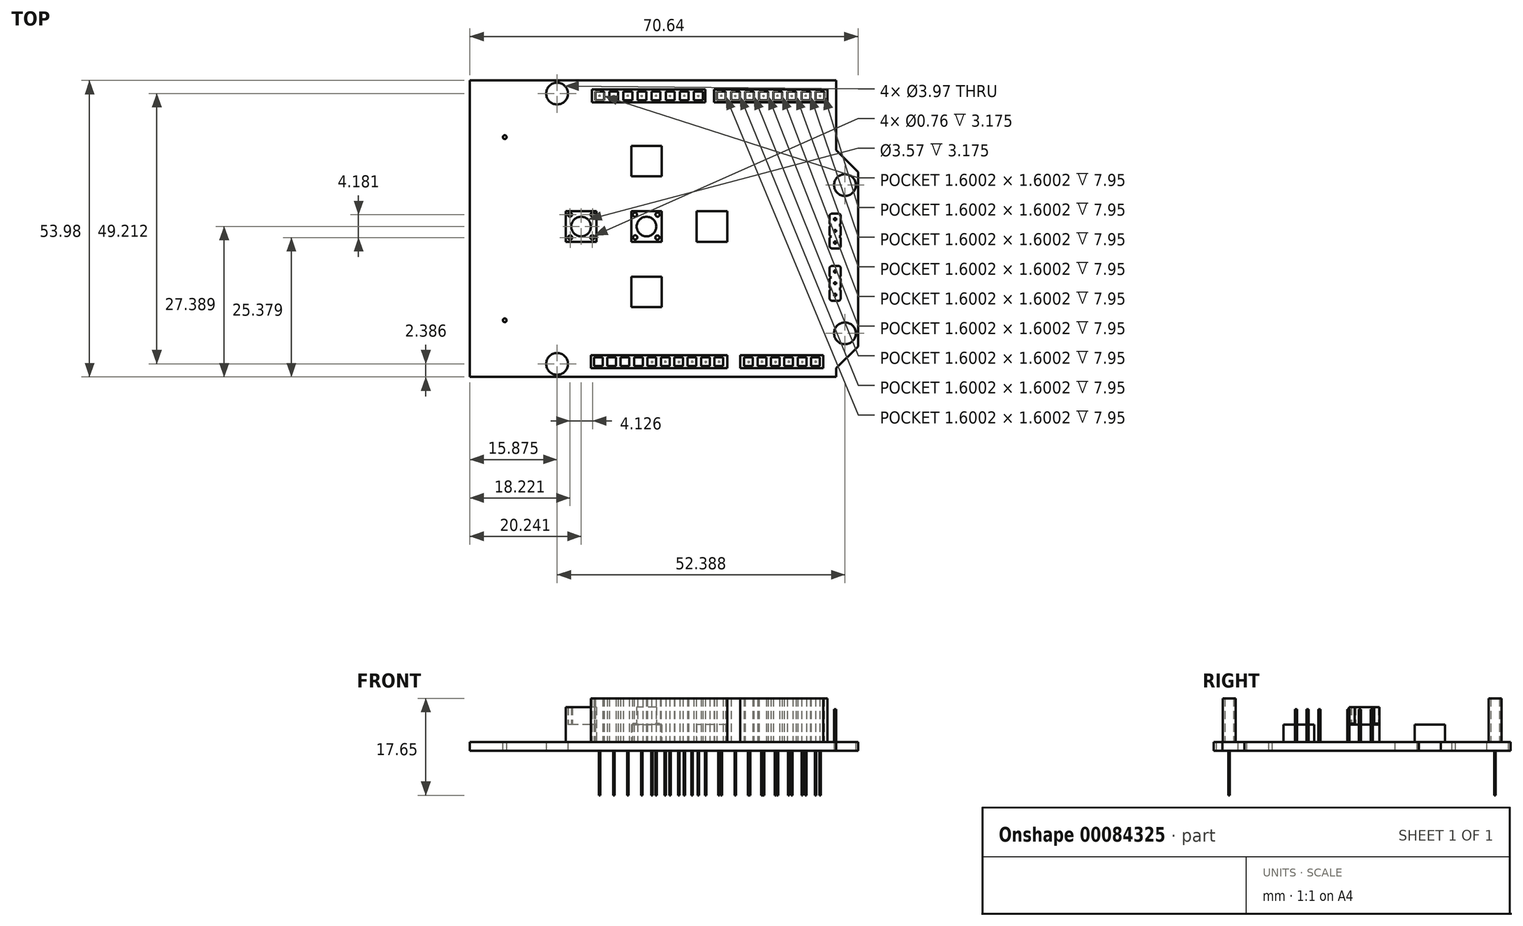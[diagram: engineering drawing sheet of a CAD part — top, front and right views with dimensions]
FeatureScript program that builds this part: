
annotation { "Feature Type Name" : "Feature", "Feature Type Description" : "" }
export const myFeature = defineFeature(function(context is Context, id is Id, definition is map)
    precondition{}
    {
        {
            var Q0;
            Q0=qCreatedBy(makeId("Top.planeOp"),FACE);
            var sketch = newSketch(context, id + "F0", { "sketchPlane" : qUnion([Q0])});
            skLineSegment(sketch, "E0.bottom", {"start": v(0, 0) * mm, "end": v(66.68, 0) * mm});
            skLineSegment(sketch, "E0.top", {"start": v(0, -53.98) * mm, "end": v(66.68, -53.98) * mm});
            skLineSegment(sketch, "E0.left", {"start": v(0, 0) * mm, "end": v(0, -53.98) * mm});
            skLineSegment(sketch, "E0.right", {"start": v(66.68, 0) * mm, "end": v(66.68, -53.97) * mm});
            skLineSegment(sketch, "E1", {"start": v(66.68, -12.7) * mm, "end": v(70.64, -16.67) * mm});
            skLineSegment(sketch, "E2", {"start": v(70.64, -16.67) * mm, "end": v(70.64, -48.42) * mm});
            skLineSegment(sketch, "E3", {"start": v(70.64, -48.42) * mm, "end": v(66.68, -52.39) * mm});
            skCircle(sketch, "E4", {"center": v(68.26, -19.05) * mm, "radius": 1.98 * mm});
            skLineSegment(sketch, "E5", {"start": v(66.68, -12.7) * mm, "end": v(68.26, -12.7) * mm, "construction": true});
            skLineSegment(sketch, "E6", {"start": v(68.26, -12.7) * mm, "end": v(68.26, -19.05) * mm, "construction": true});
            skLineSegment(sketch, "E7", {"start": v(70.64, -32.54) * mm, "end": v(66.68, -32.54) * mm});
            skCircle(sketch, "E8.MirrorC", {"center": v(68.26, -46.04) * mm, "radius": 1.98 * mm});
            skCircle(sketch, "E9", {"center": v(15.88, -2.38) * mm, "radius": 1.98 * mm});
            skLineSegment(sketch, "E10", {"start": v(0, -26.99) * mm, "end": v(15.88, -26.99) * mm, "construction": true});
            skCircle(sketch, "E11.MirrorC", {"center": v(15.88, -51.6) * mm, "radius": 1.98 * mm});
            skSolve(sketch);
        }
        {
            var Q0;
            {var subQ7=sQuery(id+"F0.wireOp",EDGE,"E0.bottom");Q0=makeQuery(id+"F0.imprint","IMPRINT",FACE,{"disambiguationData":[TD([[makeQuery(id+"F0.imprint","IMPRINT",EDGE,{"derivedFrom":subQ7}),-1.0]])]});}
            var Q1;
            {var subQ1=sQuery(id+"F0.wireOp",EDGE,"E1");Q1=makeQuery(id+"F0.imprint","IMPRINT",FACE,{"disambiguationData":[TD([[makeQuery(id+"F0.imprint","IMPRINT",EDGE,{"derivedFrom":subQ1}),-1.0]])]});}
            var Q2;
            {var subQ0=sQuery(id+"F0.wireOp",EDGE,"E3");Q2=makeQuery(id+"F0.imprint","IMPRINT",FACE,{"disambiguationData":[TD([[makeQuery(id+"F0.imprint","IMPRINT",EDGE,{"derivedFrom":subQ0}),-1.0]])]});}
            extrude(context, id + "F1", {"entities" : qUnion([Q0, Q1, Q2]), "depth" : 1.6 * mm});
        }
        {
            var Q0;
            Q0=makeQuery(id+"F1.opExtrude","CAP_FACE",FACE,{"disambiguationData":[OSD([sQuery(id+"F0.wireOp",EDGE,"E0.bottom"),sQuery(id+"F0.wireOp",EDGE,"E0.top"),sQuery(id+"F0.wireOp",EDGE,"E0.left"),sQuery(id+"F0.wireOp",EDGE,"E0.right"),sQuery(id+"F0.wireOp",EDGE,"E1"),sQuery(id+"F0.wireOp",EDGE,"E2"),sQuery(id+"F0.wireOp",EDGE,"E3"),sQuery(id+"F0.wireOp",EDGE,"E4"),sQuery(id+"F0.wireOp",EDGE,"E8.MirrorC"),sQuery(id+"F0.wireOp",EDGE,"E9"),sQuery(id+"F0.wireOp",EDGE,"E11.MirrorC")])],"isStart":false});
            var sketch = newSketch(context, id + "F2", { "sketchPlane" : qUnion([Q0])});
            skLineSegment(sketch, "E12.bottom", {"start": v(22.24, -1.6) * mm, "end": v(42.88, -1.6) * mm});
            skLineSegment(sketch, "E12.top", {"start": v(22.24, -3.99) * mm, "end": v(42.88, -3.99) * mm});
            skLineSegment(sketch, "E12.left", {"start": v(22.24, -1.6) * mm, "end": v(22.24, -3.99) * mm});
            skLineSegment(sketch, "E12.right", {"start": v(42.88, -1.6) * mm, "end": v(42.88, -3.99) * mm});
            skLineSegment(sketch, "E13.bottom", {"start": v(22.82, -2) * mm, "end": v(24.42, -2) * mm});
            skLineSegment(sketch, "E13.top", {"start": v(22.82, -3.6) * mm, "end": v(24.42, -3.6) * mm});
            skLineSegment(sketch, "E13.left", {"start": v(22.82, -2) * mm, "end": v(22.82, -3.6) * mm});
            skLineSegment(sketch, "E13.right", {"start": v(24.42, -2) * mm, "end": v(24.42, -3.6) * mm});
            skLineSegment(sketch, "E14", {"start": v(24.9, -1.6) * mm, "end": v(24.9, -3.99) * mm, "construction": true});
            skLineSegment(sketch, "E15.MirrorCS", {"start": v(25.39, -2) * mm, "end": v(25.39, -3.6) * mm});
            skLineSegment(sketch, "E16.MirrorCS", {"start": v(26.99, -2) * mm, "end": v(25.39, -2) * mm});
            skLineSegment(sketch, "E17.MirrorCS", {"start": v(26.99, -2) * mm, "end": v(26.99, -3.6) * mm});
            skLineSegment(sketch, "E18.MirrorCS", {"start": v(26.99, -3.6) * mm, "end": v(25.39, -3.6) * mm});
            skLineSegment(sketch, "E19", {"start": v(27.47, -1.6) * mm, "end": v(27.47, -3.99) * mm, "construction": true});
            skLineSegment(sketch, "E20.MirrorCS", {"start": v(27.95, -2) * mm, "end": v(27.95, -3.6) * mm});
            skLineSegment(sketch, "E21.MirrorCS", {"start": v(27.95, -2) * mm, "end": v(29.55, -2) * mm});
            skLineSegment(sketch, "E22.MirrorCS", {"start": v(29.55, -2) * mm, "end": v(29.55, -3.6) * mm});
            skLineSegment(sketch, "E23.MirrorCS", {"start": v(27.95, -3.6) * mm, "end": v(29.55, -3.6) * mm});
            skLineSegment(sketch, "E24.MirrorCS", {"start": v(30.52, -2) * mm, "end": v(30.52, -3.6) * mm});
            skLineSegment(sketch, "E25.MirrorCS", {"start": v(32.12, -2) * mm, "end": v(30.52, -2) * mm});
            skLineSegment(sketch, "E26.MirrorCS", {"start": v(32.12, -2) * mm, "end": v(32.12, -3.6) * mm});
            skLineSegment(sketch, "E27.MirrorCS", {"start": v(32.12, -3.6) * mm, "end": v(30.52, -3.6) * mm});
            skLineSegment(sketch, "E28", {"start": v(32.6, -1.6) * mm, "end": v(32.6, -3.99) * mm, "construction": true});
            skLineSegment(sketch, "E29.MirrorCS", {"start": v(33.08, -2) * mm, "end": v(33.08, -3.6) * mm});
            skLineSegment(sketch, "E30.MirrorCS", {"start": v(33.08, -2) * mm, "end": v(34.68, -2) * mm});
            skLineSegment(sketch, "E31.MirrorCS", {"start": v(34.68, -2) * mm, "end": v(34.68, -3.6) * mm});
            skLineSegment(sketch, "E32.MirrorCS", {"start": v(33.08, -3.6) * mm, "end": v(34.68, -3.6) * mm});
            skLineSegment(sketch, "E33.MirrorCS", {"start": v(35.65, -2) * mm, "end": v(35.65, -3.6) * mm});
            skLineSegment(sketch, "E34.MirrorCS", {"start": v(37.25, -2) * mm, "end": v(35.65, -2) * mm});
            skLineSegment(sketch, "E35.MirrorCS", {"start": v(37.25, -2) * mm, "end": v(37.25, -3.6) * mm});
            skLineSegment(sketch, "E36.MirrorCS", {"start": v(37.25, -3.6) * mm, "end": v(35.65, -3.6) * mm});
            skLineSegment(sketch, "E37.MirrorCS", {"start": v(38.21, -2) * mm, "end": v(38.21, -3.6) * mm});
            skLineSegment(sketch, "E38.MirrorCS", {"start": v(38.21, -2) * mm, "end": v(39.81, -2) * mm});
            skLineSegment(sketch, "E39.MirrorCS", {"start": v(39.81, -2) * mm, "end": v(39.81, -3.6) * mm});
            skLineSegment(sketch, "E40.MirrorCS", {"start": v(38.21, -3.6) * mm, "end": v(39.81, -3.6) * mm});
            skLineSegment(sketch, "E41.MirrorCS", {"start": v(40.78, -2) * mm, "end": v(40.78, -3.6) * mm});
            skLineSegment(sketch, "E42.MirrorCS", {"start": v(42.38, -2) * mm, "end": v(40.78, -2) * mm});
            skLineSegment(sketch, "E43.MirrorCS", {"start": v(42.38, -2) * mm, "end": v(42.38, -3.6) * mm});
            skLineSegment(sketch, "E44.MirrorCS", {"start": v(42.38, -3.6) * mm, "end": v(40.78, -3.6) * mm});
            skLineSegment(sketch, "E45", {"start": v(43.67, -3.99) * mm, "end": v(43.67, -6.48) * mm, "construction": true});
            skLineSegment(sketch, "E46.MirrorCS", {"start": v(44.46, -1.6) * mm, "end": v(44.46, -3.99) * mm});
            skLineSegment(sketch, "E47.MirrorCS", {"start": v(65.1, -1.6) * mm, "end": v(65.1, -3.99) * mm});
            skLineSegment(sketch, "E48.MirrorCS", {"start": v(65.1, -1.6) * mm, "end": v(44.46, -1.6) * mm});
            skLineSegment(sketch, "E49.MirrorCS", {"start": v(65.1, -3.99) * mm, "end": v(44.46, -3.99) * mm});
            skLineSegment(sketch, "E50.MirrorCS", {"start": v(44.96, -3.6) * mm, "end": v(46.56, -3.6) * mm});
            skLineSegment(sketch, "E51.MirrorCS", {"start": v(44.96, -2) * mm, "end": v(44.96, -3.6) * mm});
            skLineSegment(sketch, "E52.MirrorCS", {"start": v(44.96, -2) * mm, "end": v(46.56, -2) * mm});
            skLineSegment(sketch, "E53.MirrorCS", {"start": v(46.56, -2) * mm, "end": v(46.56, -3.6) * mm});
            skLineSegment(sketch, "E54.MirrorCS", {"start": v(47.52, -2) * mm, "end": v(47.52, -3.6) * mm});
            skLineSegment(sketch, "E55.MirrorCS", {"start": v(49.12, -2) * mm, "end": v(47.52, -2) * mm});
            skLineSegment(sketch, "E56.MirrorCS", {"start": v(49.12, -2) * mm, "end": v(49.12, -3.6) * mm});
            skLineSegment(sketch, "E57.MirrorCS", {"start": v(49.12, -3.6) * mm, "end": v(47.52, -3.6) * mm});
            skLineSegment(sketch, "E58.MirrorCS", {"start": v(50.09, -2) * mm, "end": v(50.09, -3.6) * mm});
            skLineSegment(sketch, "E59.MirrorCS", {"start": v(50.09, -2) * mm, "end": v(51.69, -2) * mm});
            skLineSegment(sketch, "E60.MirrorCS", {"start": v(51.69, -2) * mm, "end": v(51.69, -3.6) * mm});
            skLineSegment(sketch, "E61.MirrorCS", {"start": v(50.09, -3.6) * mm, "end": v(51.69, -3.6) * mm});
            skLineSegment(sketch, "E62.MirrorCS", {"start": v(52.65, -2) * mm, "end": v(52.65, -3.6) * mm});
            skLineSegment(sketch, "E63.MirrorCS", {"start": v(54.25, -2) * mm, "end": v(52.65, -2) * mm});
            skLineSegment(sketch, "E64.MirrorCS", {"start": v(54.25, -2) * mm, "end": v(54.25, -3.6) * mm});
            skLineSegment(sketch, "E65.MirrorCS", {"start": v(54.25, -3.6) * mm, "end": v(52.65, -3.6) * mm});
            skLineSegment(sketch, "E66.MirrorCS", {"start": v(55.22, -2) * mm, "end": v(55.22, -3.6) * mm});
            skLineSegment(sketch, "E67.MirrorCS", {"start": v(55.22, -2) * mm, "end": v(56.82, -2) * mm});
            skLineSegment(sketch, "E68.MirrorCS", {"start": v(56.82, -2) * mm, "end": v(56.82, -3.6) * mm});
            skLineSegment(sketch, "E69.MirrorCS", {"start": v(55.22, -3.6) * mm, "end": v(56.82, -3.6) * mm});
            skLineSegment(sketch, "E70.MirrorCS", {"start": v(57.79, -2) * mm, "end": v(57.79, -3.6) * mm});
            skLineSegment(sketch, "E71.MirrorCS", {"start": v(59.39, -2) * mm, "end": v(57.79, -2) * mm});
            skLineSegment(sketch, "E72.MirrorCS", {"start": v(59.39, -2) * mm, "end": v(59.39, -3.6) * mm});
            skLineSegment(sketch, "E73.MirrorCS", {"start": v(59.39, -3.6) * mm, "end": v(57.79, -3.6) * mm});
            skLineSegment(sketch, "E74.MirrorCS", {"start": v(60.35, -2) * mm, "end": v(60.35, -3.6) * mm});
            skLineSegment(sketch, "E75.MirrorCS", {"start": v(60.35, -2) * mm, "end": v(61.95, -2) * mm});
            skLineSegment(sketch, "E76.MirrorCS", {"start": v(61.95, -2) * mm, "end": v(61.95, -3.6) * mm});
            skLineSegment(sketch, "E77.MirrorCS", {"start": v(60.35, -3.6) * mm, "end": v(61.95, -3.6) * mm});
            skLineSegment(sketch, "E78.MirrorCS", {"start": v(62.92, -2) * mm, "end": v(62.92, -3.6) * mm});
            skLineSegment(sketch, "E79.MirrorCS", {"start": v(64.52, -2) * mm, "end": v(62.92, -2) * mm});
            skLineSegment(sketch, "E80.MirrorCS", {"start": v(64.52, -2) * mm, "end": v(64.52, -3.6) * mm});
            skLineSegment(sketch, "E81.MirrorCS", {"start": v(64.52, -3.6) * mm, "end": v(62.92, -3.6) * mm});
            skSolve(sketch);
        }
        {
            var Q0;
            Q0=makeQuery(id+"F2.imprint","IMPRINT",FACE,{"disambiguationData":[TD([[makeQuery(id+"F2.imprint","IMPRINT",EDGE,{"derivedFrom":sQuery(id+"F2.wireOp",EDGE,"E12.bottom")}),-1.0]])]});
            var Q1;
            Q1=makeQuery(id+"F2.imprint","IMPRINT",FACE,{"disambiguationData":[TD([[makeQuery(id+"F2.imprint","IMPRINT",EDGE,{"derivedFrom":sQuery(id+"F2.wireOp",EDGE,"E46.MirrorCS")}),1.0]])]});
            extrude(context, id + "F3", {"entities" : qUnion([Q0, Q1]), "operationType" : NewBodyOperationType.ADD, "depth" : 7.95 * mm});
        }
        {
            var Q0;
            {var subQ0=sQuery(id+"F0.wireOp",EDGE,"E8.MirrorC");var subQ1=sQuery(id+"F0.wireOp",EDGE,"E3");var subQ2=sQuery(id+"F0.wireOp",EDGE,"E2");var subQ3=sQuery(id+"F0.wireOp",EDGE,"E1");var subQ4=sQuery(id+"F0.wireOp",EDGE,"E0.right");var subQ5=sQuery(id+"F0.wireOp",EDGE,"E0.top");var subQ6=sQuery(id+"F0.wireOp",EDGE,"E0.bottom");var subQ7=sQuery(id+"F0.wireOp",EDGE,"E4");var subQ8=sQuery(id+"F0.wireOp",EDGE,"E0.left");var subQ9=sQuery(id+"F0.wireOp",EDGE,"E9");var subQ10=sQuery(id+"F0.wireOp",EDGE,"E11.MirrorC");Q0=makeQuery(id+"F3.boolean.opBoolean","SPLIT",FACE,{"disambiguationData":[TD([makeQuery(id+"F1.opExtrude","SWEPT_FACE",FACE,{"disambiguationData":[OSD([subQ6])]})])],"derivedFrom":makeQuery(id+"F1.opExtrude","CAP_FACE",FACE,{"disambiguationData":[OSD([subQ6,subQ5,subQ8,subQ4,subQ3,subQ2,subQ1,subQ7,subQ0,subQ9,subQ10])],"isStart":false})});}
            var sketch = newSketch(context, id + "F4", { "sketchPlane" : qUnion([Q0])});
            skLineSegment(sketch, "E82.bottom", {"start": v(31.74, -50) * mm, "end": v(46.82, -50) * mm});
            skLineSegment(sketch, "E82.top", {"start": v(31.74, -52.37) * mm, "end": v(46.82, -52.37) * mm});
            skLineSegment(sketch, "E82.right", {"start": v(46.82, -50) * mm, "end": v(46.82, -52.37) * mm});
            skLineSegment(sketch, "E83", {"start": v(48.02, -39.59) * mm, "end": v(48.02, -44.92) * mm, "construction": true});
            skLineSegment(sketch, "E84.MirrorCS", {"start": v(64.29, -50) * mm, "end": v(49.2, -50) * mm});
            skLineSegment(sketch, "E85.MirrorCS", {"start": v(49.2, -50) * mm, "end": v(49.2, -52.37) * mm});
            skLineSegment(sketch, "E86.MirrorCS", {"start": v(64.29, -52.37) * mm, "end": v(49.2, -52.37) * mm});
            skLineSegment(sketch, "E87.MirrorCS", {"start": v(64.29, -50) * mm, "end": v(64.29, -52.37) * mm});
            skLineSegment(sketch, "E88.bottom", {"start": v(32.34, -50.4) * mm, "end": v(33.93, -50.4) * mm});
            skLineSegment(sketch, "E88.top", {"start": v(32.34, -51.98) * mm, "end": v(33.93, -51.98) * mm});
            skLineSegment(sketch, "E88.left", {"start": v(32.34, -50.4) * mm, "end": v(32.34, -51.98) * mm});
            skLineSegment(sketch, "E88.right", {"start": v(33.93, -50.4) * mm, "end": v(33.93, -51.98) * mm});
            skLineSegment(sketch, "E89.bottom", {"start": v(34.76, -50.4) * mm, "end": v(36.35, -50.4) * mm});
            skLineSegment(sketch, "E89.top", {"start": v(34.76, -51.98) * mm, "end": v(36.35, -51.98) * mm});
            skLineSegment(sketch, "E89.left", {"start": v(34.76, -50.4) * mm, "end": v(34.76, -51.98) * mm});
            skLineSegment(sketch, "E89.right", {"start": v(36.35, -50.4) * mm, "end": v(36.35, -51.98) * mm});
            skLineSegment(sketch, "E90", {"start": v(36.78, -50) * mm, "end": v(36.78, -52.37) * mm, "construction": true});
            skLineSegment(sketch, "E91.MirrorCS", {"start": v(38.8, -50.4) * mm, "end": v(37.22, -50.4) * mm});
            skLineSegment(sketch, "E92.MirrorCS", {"start": v(37.22, -50.4) * mm, "end": v(37.22, -51.98) * mm});
            skLineSegment(sketch, "E93.MirrorCS", {"start": v(38.8, -51.98) * mm, "end": v(37.22, -51.98) * mm});
            skLineSegment(sketch, "E94.MirrorCS", {"start": v(38.8, -50.4) * mm, "end": v(38.8, -51.98) * mm});
            skLineSegment(sketch, "E95.MirrorCS", {"start": v(39.64, -50.4) * mm, "end": v(39.64, -51.98) * mm});
            skLineSegment(sketch, "E96.MirrorCS", {"start": v(41.23, -50.4) * mm, "end": v(39.64, -50.4) * mm});
            skLineSegment(sketch, "E97.MirrorCS", {"start": v(41.23, -50.4) * mm, "end": v(41.23, -51.98) * mm});
            skLineSegment(sketch, "E98.MirrorCS", {"start": v(41.23, -51.98) * mm, "end": v(39.64, -51.98) * mm});
            skLineSegment(sketch, "E99", {"start": v(41.66, -50) * mm, "end": v(41.66, -52.37) * mm, "construction": true});
            skLineSegment(sketch, "E100.MirrorCS", {"start": v(42.1, -50.4) * mm, "end": v(43.68, -50.4) * mm});
            skLineSegment(sketch, "E101.MirrorCS", {"start": v(42.1, -50.4) * mm, "end": v(42.1, -51.98) * mm});
            skLineSegment(sketch, "E102.MirrorCS", {"start": v(42.1, -51.98) * mm, "end": v(43.68, -51.98) * mm});
            skLineSegment(sketch, "E103.MirrorCS", {"start": v(43.68, -50.4) * mm, "end": v(43.68, -51.98) * mm});
            skLineSegment(sketch, "E104.MirrorCS", {"start": v(44.52, -50.4) * mm, "end": v(44.52, -51.98) * mm});
            skLineSegment(sketch, "E105.MirrorCS", {"start": v(44.52, -50.4) * mm, "end": v(46.1, -50.4) * mm});
            skLineSegment(sketch, "E106.MirrorCS", {"start": v(46.1, -50.4) * mm, "end": v(46.1, -51.98) * mm});
            skLineSegment(sketch, "E107.MirrorCS", {"start": v(44.52, -51.98) * mm, "end": v(46.1, -51.98) * mm});
            skLineSegment(sketch, "E108.MirrorCS", {"start": v(49.93, -50.4) * mm, "end": v(49.93, -51.98) * mm});
            skLineSegment(sketch, "E109.MirrorCS", {"start": v(51.51, -50.4) * mm, "end": v(49.93, -50.4) * mm});
            skLineSegment(sketch, "E110.MirrorCS", {"start": v(51.51, -50.4) * mm, "end": v(51.51, -51.98) * mm});
            skLineSegment(sketch, "E111.MirrorCS", {"start": v(51.51, -51.98) * mm, "end": v(49.93, -51.98) * mm});
            skLineSegment(sketch, "E112.MirrorCS", {"start": v(52.35, -50.4) * mm, "end": v(52.35, -51.98) * mm});
            skLineSegment(sketch, "E113.MirrorCS", {"start": v(53.94, -50.4) * mm, "end": v(52.35, -50.4) * mm});
            skLineSegment(sketch, "E114.MirrorCS", {"start": v(53.94, -50.4) * mm, "end": v(53.94, -51.98) * mm});
            skLineSegment(sketch, "E115.MirrorCS", {"start": v(53.94, -51.98) * mm, "end": v(52.35, -51.98) * mm});
            skLineSegment(sketch, "E116.MirrorCS", {"start": v(54.8, -50.4) * mm, "end": v(56.39, -50.4) * mm});
            skLineSegment(sketch, "E117.MirrorCS", {"start": v(54.8, -50.4) * mm, "end": v(54.8, -51.98) * mm});
            skLineSegment(sketch, "E118.MirrorCS", {"start": v(54.8, -51.98) * mm, "end": v(56.39, -51.98) * mm});
            skLineSegment(sketch, "E119.MirrorCS", {"start": v(56.39, -50.4) * mm, "end": v(56.39, -51.98) * mm});
            skLineSegment(sketch, "E120.MirrorCS", {"start": v(57.23, -50.4) * mm, "end": v(57.23, -51.98) * mm});
            skLineSegment(sketch, "E121.MirrorCS", {"start": v(57.23, -50.4) * mm, "end": v(58.82, -50.4) * mm});
            skLineSegment(sketch, "E122.MirrorCS", {"start": v(58.82, -50.4) * mm, "end": v(58.82, -51.98) * mm});
            skLineSegment(sketch, "E123.MirrorCS", {"start": v(57.23, -51.98) * mm, "end": v(58.82, -51.98) * mm});
            skLineSegment(sketch, "E124.MirrorCS", {"start": v(59.68, -50.4) * mm, "end": v(59.68, -51.98) * mm});
            skLineSegment(sketch, "E125.MirrorCS", {"start": v(61.27, -50.4) * mm, "end": v(59.68, -50.4) * mm});
            skLineSegment(sketch, "E126.MirrorCS", {"start": v(61.27, -50.4) * mm, "end": v(61.27, -51.98) * mm});
            skLineSegment(sketch, "E127.MirrorCS", {"start": v(61.27, -51.98) * mm, "end": v(59.68, -51.98) * mm});
            skLineSegment(sketch, "E128.MirrorCS", {"start": v(62.1, -50.4) * mm, "end": v(62.1, -51.98) * mm});
            skLineSegment(sketch, "E129.MirrorCS", {"start": v(63.7, -50.4) * mm, "end": v(62.1, -50.4) * mm});
            skLineSegment(sketch, "E130.MirrorCS", {"start": v(63.7, -50.4) * mm, "end": v(63.7, -51.98) * mm});
            skLineSegment(sketch, "E131.MirrorCS", {"start": v(63.7, -51.98) * mm, "end": v(62.1, -51.98) * mm});
            skLineSegment(sketch, "E132", {"start": v(31.9, -50) * mm, "end": v(31.9, -52.37) * mm, "construction": true});
            skLineSegment(sketch, "E133.MirrorCS", {"start": v(31.46, -50.4) * mm, "end": v(31.46, -51.98) * mm});
            skLineSegment(sketch, "E134.MirrorCS", {"start": v(31.46, -50.4) * mm, "end": v(29.88, -50.4) * mm});
            skLineSegment(sketch, "E135.MirrorCS", {"start": v(29.88, -50.4) * mm, "end": v(29.88, -51.98) * mm});
            skLineSegment(sketch, "E136.MirrorCS", {"start": v(31.46, -51.98) * mm, "end": v(29.88, -51.98) * mm});
            skLineSegment(sketch, "E137.MirrorCS", {"start": v(29.04, -50.4) * mm, "end": v(29.04, -51.98) * mm});
            skLineSegment(sketch, "E138.MirrorCS", {"start": v(29.04, -50.4) * mm, "end": v(27.45, -50.4) * mm});
            skLineSegment(sketch, "E139.MirrorCS", {"start": v(27.45, -50.4) * mm, "end": v(27.45, -51.98) * mm});
            skLineSegment(sketch, "E140.MirrorCS", {"start": v(29.04, -51.98) * mm, "end": v(27.45, -51.98) * mm});
            skLineSegment(sketch, "E141.MirrorCS", {"start": v(26.59, -50.4) * mm, "end": v(26.59, -51.98) * mm});
            skLineSegment(sketch, "E142.MirrorCS", {"start": v(25, -50.4) * mm, "end": v(26.59, -50.4) * mm});
            skLineSegment(sketch, "E143.MirrorCS", {"start": v(25, -50.4) * mm, "end": v(25, -51.98) * mm});
            skLineSegment(sketch, "E144.MirrorCS", {"start": v(25, -51.98) * mm, "end": v(26.59, -51.98) * mm});
            skLineSegment(sketch, "E145.MirrorCS", {"start": v(24.16, -50.4) * mm, "end": v(24.16, -51.98) * mm});
            skLineSegment(sketch, "E146.MirrorCS", {"start": v(22.57, -50.4) * mm, "end": v(24.16, -50.4) * mm});
            skLineSegment(sketch, "E147.MirrorCS", {"start": v(22.57, -50.4) * mm, "end": v(22.57, -51.98) * mm});
            skLineSegment(sketch, "E148.MirrorCS", {"start": v(22.57, -51.98) * mm, "end": v(24.16, -51.98) * mm});
            skLineSegment(sketch, "E149", {"start": v(31.74, -50) * mm, "end": v(22, -50) * mm});
            skLineSegment(sketch, "E150", {"start": v(31.74, -52.37) * mm, "end": v(22, -52.37) * mm});
            skLineSegment(sketch, "E151", {"start": v(22, -50) * mm, "end": v(22, -52.37) * mm});
            skSolve(sketch);
        }
        {
            var Q0;
            Q0=makeQuery(id+"F4.imprint","IMPRINT",FACE,{"disambiguationData":[TD([[makeQuery(id+"F4.imprint","IMPRINT",EDGE,{"derivedFrom":sQuery(id+"F4.wireOp",EDGE,"E82.bottom")}),-1.0]])]});
            var Q1;
            Q1=makeQuery(id+"F4.imprint","IMPRINT",FACE,{"disambiguationData":[TD([[makeQuery(id+"F4.imprint","IMPRINT",EDGE,{"derivedFrom":sQuery(id+"F4.wireOp",EDGE,"E84.MirrorCS")}),1.0]])]});
            extrude(context, id + "F5", {"entities" : qUnion([Q0, Q1]), "operationType" : NewBodyOperationType.ADD, "depth" : 7.95 * mm});
        }
        {
            var Q0;
            {var subQ4=sQuery(id+"F0.wireOp",EDGE,"E0.top");var subQ6=sQuery(id+"F0.wireOp",EDGE,"E11.MirrorC");var subQ8=sQuery(id+"F0.wireOp",EDGE,"E9");var subQ10=sQuery(id+"F0.wireOp",EDGE,"E0.right");var subQ11=sQuery(id+"F0.wireOp",EDGE,"E0.bottom");var subQ12=sQuery(id+"F0.wireOp",EDGE,"E1");var subQ15=makeQuery(id+"F1.opExtrude","SWEPT_FACE",FACE,{"disambiguationData":[OSD([subQ11])]});var subQ16=sQuery(id+"F0.wireOp",EDGE,"E0.left");var subQ19=sQuery(id+"F0.wireOp",EDGE,"E4");var subQ23=sQuery(id+"F0.wireOp",EDGE,"E3");var subQ26=sQuery(id+"F0.wireOp",EDGE,"E2");var subQ29=sQuery(id+"F0.wireOp",EDGE,"E8.MirrorC");Q0=makeQuery(id+"F5.boolean.opBoolean","SPLIT",FACE,{"disambiguationData":[TD([subQ15])],"derivedFrom":makeQuery(id+"F3.boolean.opBoolean","SPLIT",FACE,{"disambiguationData":[TD([subQ15])],"derivedFrom":makeQuery(id+"F1.opExtrude","CAP_FACE",FACE,{"disambiguationData":[OSD([subQ11,subQ4,subQ16,subQ10,subQ12,subQ26,subQ23,subQ19,subQ29,subQ8,subQ6])],"isStart":false})})});}
            var sketch = newSketch(context, id + "F6", { "sketchPlane" : qUnion([Q0])});
            skLineSegment(sketch, "E152.bottom", {"start": v(65.48, -24.2) * mm, "end": v(67.47, -24.2) * mm});
            skLineSegment(sketch, "E152.top", {"start": v(65.48, -30.56) * mm, "end": v(67.47, -30.56) * mm});
            skLineSegment(sketch, "E152.left", {"start": v(65.48, -24.2) * mm, "end": v(65.48, -30.56) * mm});
            skLineSegment(sketch, "E152.right", {"start": v(67.47, -24.2) * mm, "end": v(67.47, -30.56) * mm});
            skLineSegment(sketch, "E153", {"start": v(67.2, -24.2) * mm, "end": v(67.47, -24.47) * mm});
            skLineSegment(sketch, "E154", {"start": v(67.47, -26.06) * mm, "end": v(67.2, -26.32) * mm});
            skLineSegment(sketch, "E155", {"start": v(67.2, -26.32) * mm, "end": v(67.47, -26.59) * mm});
            skLineSegment(sketch, "E156", {"start": v(67.47, -28.17) * mm, "end": v(67.2, -28.44) * mm});
            skLineSegment(sketch, "E157", {"start": v(67.2, -28.44) * mm, "end": v(67.47, -28.7) * mm});
            skLineSegment(sketch, "E158", {"start": v(67.47, -30.3) * mm, "end": v(67.2, -30.56) * mm});
            skLineSegment(sketch, "E159", {"start": v(66.48, -24.2) * mm, "end": v(66.48, -30.56) * mm, "construction": true});
            skLineSegment(sketch, "E160.MirrorCS", {"start": v(65.75, -24.2) * mm, "end": v(65.48, -24.47) * mm});
            skLineSegment(sketch, "E161.MirrorCS", {"start": v(65.48, -26.06) * mm, "end": v(65.75, -26.32) * mm});
            skLineSegment(sketch, "E162.MirrorCS", {"start": v(65.75, -26.32) * mm, "end": v(65.48, -26.59) * mm});
            skLineSegment(sketch, "E163.MirrorCS", {"start": v(65.48, -28.17) * mm, "end": v(65.75, -28.44) * mm});
            skLineSegment(sketch, "E164.MirrorCS", {"start": v(65.75, -28.44) * mm, "end": v(65.48, -28.7) * mm});
            skLineSegment(sketch, "E165.MirrorCS", {"start": v(65.48, -30.3) * mm, "end": v(65.75, -30.56) * mm});
            skLineSegment(sketch, "E166", {"start": v(70.64, -32.14) * mm, "end": v(63.46, -32.14) * mm, "construction": true});
            skLineSegment(sketch, "E167.MirrorCS", {"start": v(65.48, -33.73) * mm, "end": v(67.47, -33.73) * mm});
            skLineSegment(sketch, "E168.MirrorCS", {"start": v(65.48, -40.08) * mm, "end": v(65.48, -33.73) * mm});
            skLineSegment(sketch, "E169.MirrorCS", {"start": v(65.48, -34) * mm, "end": v(65.75, -33.73) * mm});
            skLineSegment(sketch, "E170.MirrorCS", {"start": v(67.47, -34) * mm, "end": v(67.2, -33.73) * mm});
            skLineSegment(sketch, "E171.MirrorCS", {"start": v(67.47, -40.08) * mm, "end": v(67.47, -33.73) * mm});
            skLineSegment(sketch, "E172.MirrorCS", {"start": v(65.75, -35.85) * mm, "end": v(65.48, -35.58) * mm});
            skLineSegment(sketch, "E173.MirrorCS", {"start": v(65.48, -36.11) * mm, "end": v(65.75, -35.85) * mm});
            skLineSegment(sketch, "E174.MirrorCS", {"start": v(67.2, -35.85) * mm, "end": v(67.47, -35.58) * mm});
            skLineSegment(sketch, "E175.MirrorCS", {"start": v(67.47, -36.11) * mm, "end": v(67.2, -35.85) * mm});
            skLineSegment(sketch, "E176.MirrorCS", {"start": v(67.2, -37.96) * mm, "end": v(67.47, -37.7) * mm});
            skLineSegment(sketch, "E177.MirrorCS", {"start": v(67.47, -38.23) * mm, "end": v(67.2, -37.96) * mm});
            skLineSegment(sketch, "E178.MirrorCS", {"start": v(65.48, -38.23) * mm, "end": v(65.75, -37.96) * mm});
            skLineSegment(sketch, "E179.MirrorCS", {"start": v(65.75, -37.96) * mm, "end": v(65.48, -37.7) * mm});
            skLineSegment(sketch, "E180.MirrorCS", {"start": v(65.75, -40.08) * mm, "end": v(65.48, -39.82) * mm});
            skLineSegment(sketch, "E181.MirrorCS", {"start": v(65.48, -40.08) * mm, "end": v(67.47, -40.08) * mm});
            skLineSegment(sketch, "E182.MirrorCS", {"start": v(67.2, -40.08) * mm, "end": v(67.47, -39.82) * mm});
            skSolve(sketch);
        }
        {
            var Q0;
            {var subQ3=sQuery(id+"F6.wireOp",EDGE,"E169.MirrorCS");Q0=makeQuery(id+"F6.imprint","IMPRINT",FACE,{"disambiguationData":[TD([[makeQuery(id+"F6.imprint","IMPRINT",EDGE,{"derivedFrom":subQ3}),-1.0]])]});}
            var Q1;
            {var subQ1=sQuery(id+"F6.wireOp",EDGE,"E153");Q1=makeQuery(id+"F6.imprint","IMPRINT",FACE,{"disambiguationData":[TD([[makeQuery(id+"F6.imprint","IMPRINT",EDGE,{"derivedFrom":subQ1}),-1.0]])]});}
            extrude(context, id + "F7", {"entities" : qUnion([Q0, Q1]), "operationType" : NewBodyOperationType.ADD, "depth" : 1.5 / 406.4 * mm});
        }
        {
            var Q0;
            Q0=makeQuery(id+"F7.opExtrude","CAP_FACE",FACE,{"disambiguationData":[OSD([sQuery(id+"F6.wireOp",EDGE,"E152.bottom"),sQuery(id+"F6.wireOp",EDGE,"E152.top"),sQuery(id+"F6.wireOp",EDGE,"E152.left"),sQuery(id+"F6.wireOp",EDGE,"E152.right"),sQuery(id+"F6.wireOp",EDGE,"E153"),sQuery(id+"F6.wireOp",EDGE,"E154"),sQuery(id+"F6.wireOp",EDGE,"E155"),sQuery(id+"F6.wireOp",EDGE,"E156"),sQuery(id+"F6.wireOp",EDGE,"E157"),sQuery(id+"F6.wireOp",EDGE,"E158"),sQuery(id+"F6.wireOp",EDGE,"E160.MirrorCS"),sQuery(id+"F6.wireOp",EDGE,"E161.MirrorCS"),sQuery(id+"F6.wireOp",EDGE,"E162.MirrorCS"),sQuery(id+"F6.wireOp",EDGE,"E163.MirrorCS"),sQuery(id+"F6.wireOp",EDGE,"E164.MirrorCS"),sQuery(id+"F6.wireOp",EDGE,"E165.MirrorCS")])],"isStart":false});
            var sketch = newSketch(context, id + "F8", { "sketchPlane" : qUnion([Q0])});
            skLineSegment(sketch, "E183", {"start": v(65.48, -25.26) * mm, "end": v(67.47, -25.26) * mm, "construction": true});
            skPoint(sketch, "E184.middle", {"position": v(66.48, -25.26) * mm});
            skLineSegment(sketch, "E185.bottom", {"start": v(66.66, -25.45) * mm, "end": v(66.29, -25.45) * mm});
            skLineSegment(sketch, "E185.top", {"start": v(66.66, -25.08) * mm, "end": v(66.29, -25.08) * mm});
            skLineSegment(sketch, "E185.left", {"start": v(66.66, -25.45) * mm, "end": v(66.66, -25.08) * mm});
            skLineSegment(sketch, "E185.right", {"start": v(66.29, -25.45) * mm, "end": v(66.29, -25.08) * mm});
            skLineSegment(sketch, "E186", {"start": v(65.75, -26.32) * mm, "end": v(67.2, -26.32) * mm, "construction": true});
            skLineSegment(sketch, "E187.MirrorCS", {"start": v(66.66, -27.2) * mm, "end": v(66.29, -27.2) * mm});
            skLineSegment(sketch, "E188.MirrorCS", {"start": v(66.66, -27.2) * mm, "end": v(66.66, -27.57) * mm});
            skLineSegment(sketch, "E189.MirrorCS", {"start": v(66.66, -27.57) * mm, "end": v(66.29, -27.57) * mm});
            skLineSegment(sketch, "E190.MirrorCS", {"start": v(66.29, -27.2) * mm, "end": v(66.29, -27.57) * mm});
            skLineSegment(sketch, "E191", {"start": v(65.75, -28.44) * mm, "end": v(67.2, -28.44) * mm, "construction": true});
            skLineSegment(sketch, "E192.MirrorCS", {"start": v(66.66, -29.31) * mm, "end": v(66.29, -29.31) * mm});
            skLineSegment(sketch, "E193.MirrorCS", {"start": v(66.66, -29.68) * mm, "end": v(66.66, -29.31) * mm});
            skLineSegment(sketch, "E194.MirrorCS", {"start": v(66.66, -29.68) * mm, "end": v(66.29, -29.68) * mm});
            skLineSegment(sketch, "E195.MirrorCS", {"start": v(66.29, -29.68) * mm, "end": v(66.29, -29.31) * mm});
            skLineSegment(sketch, "E196.MirrorCS", {"start": v(66.66, -34.6) * mm, "end": v(66.66, -34.97) * mm});
            skLineSegment(sketch, "E197.MirrorCS", {"start": v(66.66, -34.97) * mm, "end": v(66.29, -34.97) * mm});
            skLineSegment(sketch, "E198.MirrorCS", {"start": v(66.29, -34.6) * mm, "end": v(66.29, -34.97) * mm});
            skLineSegment(sketch, "E199.MirrorCS", {"start": v(66.66, -34.6) * mm, "end": v(66.29, -34.6) * mm});
            skLineSegment(sketch, "E200.MirrorCS", {"start": v(66.66, -37.1) * mm, "end": v(66.66, -36.72) * mm});
            skLineSegment(sketch, "E201.MirrorCS", {"start": v(66.66, -37.1) * mm, "end": v(66.29, -37.1) * mm});
            skLineSegment(sketch, "E202.MirrorCS", {"start": v(66.29, -37.1) * mm, "end": v(66.29, -36.72) * mm});
            skLineSegment(sketch, "E203.MirrorCS", {"start": v(66.66, -36.72) * mm, "end": v(66.29, -36.72) * mm});
            skLineSegment(sketch, "E204.MirrorCS", {"start": v(66.66, -38.84) * mm, "end": v(66.66, -39.2) * mm});
            skLineSegment(sketch, "E205.MirrorCS", {"start": v(66.66, -39.2) * mm, "end": v(66.29, -39.2) * mm});
            skLineSegment(sketch, "E206.MirrorCS", {"start": v(65.48, -39.02) * mm, "end": v(67.47, -39.02) * mm, "construction": true});
            skLineSegment(sketch, "E207.MirrorCS", {"start": v(66.29, -38.84) * mm, "end": v(66.29, -39.2) * mm});
            skLineSegment(sketch, "E208.MirrorCS", {"start": v(66.66, -38.84) * mm, "end": v(66.29, -38.84) * mm});
            skSolve(sketch);
        }
        {
            var Q0;
            Q0=makeQuery(id+"F8.imprint","IMPRINT",FACE,{"disambiguationData":[TD([[makeQuery(id+"F8.imprint","IMPRINT",EDGE,{"derivedFrom":sQuery(id+"F8.wireOp",EDGE,"E185.bottom")}),-1.0]])]});
            var Q1;
            Q1=makeQuery(id+"F8.imprint","IMPRINT",FACE,{"disambiguationData":[TD([[makeQuery(id+"F8.imprint","IMPRINT",EDGE,{"derivedFrom":sQuery(id+"F8.wireOp",EDGE,"E187.MirrorCS")}),1.0]])]});
            var Q2;
            Q2=makeQuery(id+"F8.imprint","IMPRINT",FACE,{"disambiguationData":[TD([[makeQuery(id+"F8.imprint","IMPRINT",EDGE,{"derivedFrom":sQuery(id+"F8.wireOp",EDGE,"E192.MirrorCS")}),1.0]])]});
            var Q3;
            Q3=makeQuery(id+"F8.imprint","IMPRINT",FACE,{"disambiguationData":[TD([[makeQuery(id+"F8.imprint","IMPRINT",EDGE,{"derivedFrom":sQuery(id+"F8.wireOp",EDGE,"E196.MirrorCS")}),-1.0]])]});
            var Q4;
            Q4=makeQuery(id+"F8.imprint","IMPRINT",FACE,{"disambiguationData":[TD([[makeQuery(id+"F8.imprint","IMPRINT",EDGE,{"derivedFrom":sQuery(id+"F8.wireOp",EDGE,"E200.MirrorCS")}),1.0]])]});
            var Q5;
            Q5=makeQuery(id+"F8.imprint","IMPRINT",FACE,{"disambiguationData":[TD([[makeQuery(id+"F8.imprint","IMPRINT",EDGE,{"derivedFrom":sQuery(id+"F8.wireOp",EDGE,"E204.MirrorCS")}),-1.0]])]});
            extrude(context, id + "F9", {"entities" : qUnion([Q0, Q1, Q2, Q3, Q4, Q5]), "operationType" : NewBodyOperationType.ADD, "depth" : 5.95 * mm});
        }
        {
            var Q0;
            {var subQ45=sQuery(id+"F0.wireOp",EDGE,"E0.bottom");Q0=makeQuery(id+"F6.imprint","IMPRINT",FACE,{"disambiguationData":[TD([[makeQuery(id+"F6.imprint","IMPRINT",EDGE,{"derivedFrom":makeQuery(id+"F1.opExtrude","CAP_EDGE",EDGE,{"disambiguationData":[OSD([subQ45])],"isStart":false})}),-1.0]])]});}
            var sketch = newSketch(context, id + "F10", { "sketchPlane" : qUnion([Q0])});
            skLineSegment(sketch, "E209.bottom", {"start": v(29.37, -23.81) * mm, "end": v(34.93, -23.81) * mm});
            skLineSegment(sketch, "E209.top", {"start": v(29.37, -29.37) * mm, "end": v(34.93, -29.37) * mm});
            skLineSegment(sketch, "E209.left", {"start": v(29.37, -23.81) * mm, "end": v(29.37, -29.37) * mm});
            skLineSegment(sketch, "E209.right", {"start": v(34.93, -23.81) * mm, "end": v(34.93, -29.37) * mm});
            skLineSegment(sketch, "E210", {"start": v(38.1, -23.81) * mm, "end": v(38.1, -29.37) * mm, "construction": true});
            skLineSegment(sketch, "E211", {"start": v(29.37, -20.64) * mm, "end": v(34.92, -20.64) * mm, "construction": true});
            skLineSegment(sketch, "E212", {"start": v(26.2, -23.81) * mm, "end": v(26.2, -29.37) * mm, "construction": true});
            skLineSegment(sketch, "E213", {"start": v(29.37, -32.54) * mm, "end": v(34.93, -32.54) * mm, "construction": true});
            skLineSegment(sketch, "E214.MirrorCS", {"start": v(29.37, -17.46) * mm, "end": v(34.93, -17.46) * mm});
            skLineSegment(sketch, "E215.MirrorCS", {"start": v(29.37, -17.46) * mm, "end": v(29.37, -11.9) * mm});
            skLineSegment(sketch, "E216.MirrorCS", {"start": v(29.37, -11.9) * mm, "end": v(34.92, -11.9) * mm});
            skLineSegment(sketch, "E217.MirrorCS", {"start": v(34.93, -17.46) * mm, "end": v(34.92, -11.9) * mm});
            skLineSegment(sketch, "E218.MirrorCS", {"start": v(46.83, -23.81) * mm, "end": v(41.27, -23.81) * mm});
            skLineSegment(sketch, "E219.MirrorCS", {"start": v(41.27, -23.81) * mm, "end": v(41.27, -29.37) * mm});
            skLineSegment(sketch, "E220.MirrorCS", {"start": v(46.83, -29.37) * mm, "end": v(41.27, -29.37) * mm});
            skLineSegment(sketch, "E221.MirrorCS", {"start": v(46.83, -23.81) * mm, "end": v(46.83, -29.37) * mm});
            skLineSegment(sketch, "E222.MirrorCS", {"start": v(29.37, -41.27) * mm, "end": v(29.37, -35.72) * mm});
            skLineSegment(sketch, "E223.MirrorCS", {"start": v(29.37, -35.72) * mm, "end": v(34.93, -35.72) * mm});
            skLineSegment(sketch, "E224.MirrorCS", {"start": v(34.93, -41.27) * mm, "end": v(34.93, -35.72) * mm});
            skLineSegment(sketch, "E225.MirrorCS", {"start": v(29.37, -41.27) * mm, "end": v(34.93, -41.27) * mm});
            skLineSegment(sketch, "E226.MirrorCS", {"start": v(23.02, -23.81) * mm, "end": v(23.02, -29.37) * mm});
            skLineSegment(sketch, "E227.MirrorCS", {"start": v(23.02, -23.81) * mm, "end": v(17.46, -23.81) * mm});
            skLineSegment(sketch, "E228.MirrorCS", {"start": v(17.46, -23.81) * mm, "end": v(17.46, -29.37) * mm});
            skLineSegment(sketch, "E229.MirrorCS", {"start": v(23.02, -29.37) * mm, "end": v(17.46, -29.37) * mm});
            skSolve(sketch);
        }
        {
            var Q0;
            Q0=makeQuery(id+"F10.imprint","IMPRINT",FACE,{"disambiguationData":[TD([[makeQuery(id+"F10.imprint","IMPRINT",EDGE,{"derivedFrom":sQuery(id+"F10.wireOp",EDGE,"E226.MirrorCS")}),-1.0]])]});
            var Q1;
            Q1=makeQuery(id+"F10.imprint","IMPRINT",FACE,{"disambiguationData":[TD([[makeQuery(id+"F10.imprint","IMPRINT",EDGE,{"derivedFrom":sQuery(id+"F10.wireOp",EDGE,"E214.MirrorCS")}),1.0]])]});
            var Q2;
            Q2=makeQuery(id+"F10.imprint","IMPRINT",FACE,{"disambiguationData":[TD([[makeQuery(id+"F10.imprint","IMPRINT",EDGE,{"derivedFrom":sQuery(id+"F10.wireOp",EDGE,"E209.bottom")}),-1.0]])]});
            var Q3;
            Q3=makeQuery(id+"F10.imprint","IMPRINT",FACE,{"disambiguationData":[TD([[makeQuery(id+"F10.imprint","IMPRINT",EDGE,{"derivedFrom":sQuery(id+"F10.wireOp",EDGE,"E218.MirrorCS")}),1.0]])]});
            var Q4;
            Q4=makeQuery(id+"F10.imprint","IMPRINT",FACE,{"disambiguationData":[TD([[makeQuery(id+"F10.imprint","IMPRINT",EDGE,{"derivedFrom":sQuery(id+"F10.wireOp",EDGE,"E222.MirrorCS")}),-1.0]])]});
            extrude(context, id + "F11", {"entities" : qUnion([Q0, Q1, Q2, Q3, Q4]), "operationType" : NewBodyOperationType.ADD, "depth" : 3.17 * mm});
        }
        {
            var Q0;
            Q0=makeQuery(id+"F11.opExtrude","CAP_FACE",FACE,{"disambiguationData":[OSD([sQuery(id+"F10.wireOp",EDGE,"E226.MirrorCS"),sQuery(id+"F10.wireOp",EDGE,"E227.MirrorCS"),sQuery(id+"F10.wireOp",EDGE,"E228.MirrorCS"),sQuery(id+"F10.wireOp",EDGE,"E229.MirrorCS")])],"isStart":false});
            var sketch = newSketch(context, id + "F12", { "sketchPlane" : qUnion([Q0])});
            skCircle(sketch, "E230", {"center": v(32.15, -26.6) * mm, "radius": 1.79 * mm});
            skPoint(sketch, "E230.centerSnap0", {"position": v(34.93, -26.6) * mm});
            skPoint(sketch, "E230.centerSnap1", {"position": v(32.15, -23.81) * mm});
            skCircle(sketch, "E231", {"center": v(30.04, -24.42) * mm, "radius": 0.38 * mm});
            skCircle(sketch, "E232.1.0.0", {"center": v(34.17, -24.42) * mm, "radius": 0.38 * mm});
            skLineSegment(sketch, "E232.direction1", {"start": v(30.04, -24.42) * mm, "end": v(34.17, -24.42) * mm, "construction": true});
            skCircle(sketch, "E233.1.0.0", {"center": v(34.13, -28.6) * mm, "radius": 0.38 * mm});
            skLineSegment(sketch, "E233.direction1", {"start": v(34.17, -24.42) * mm, "end": v(34.13, -28.6) * mm, "construction": true});
            skCircle(sketch, "E234.1.0.0", {"center": v(30.1, -28.58) * mm, "radius": 0.38 * mm});
            skLineSegment(sketch, "E234.direction1", {"start": v(30.04, -24.42) * mm, "end": v(30.1, -28.58) * mm, "construction": true});
            skCircle(sketch, "E235.MirrorC", {"center": v(32.15, -14.68) * mm, "radius": 1.79 * mm});
            skCircle(sketch, "E236.MirrorC", {"center": v(30.04, -16.86) * mm, "radius": 0.38 * mm});
            skCircle(sketch, "E237.MirrorC", {"center": v(34.17, -16.86) * mm, "radius": 0.38 * mm});
            skCircle(sketch, "E238.MirrorC", {"center": v(34.13, -12.67) * mm, "radius": 0.38 * mm});
            skCircle(sketch, "E239.MirrorC", {"center": v(30.1, -12.7) * mm, "radius": 0.38 * mm});
            skCircle(sketch, "E240.MirrorC", {"center": v(44.05, -26.6) * mm, "radius": 1.79 * mm});
            skCircle(sketch, "E241.MirrorC", {"center": v(42.03, -24.42) * mm, "radius": 0.38 * mm});
            skCircle(sketch, "E242.MirrorC", {"center": v(46.16, -24.42) * mm, "radius": 0.38 * mm});
            skCircle(sketch, "E243.MirrorC", {"center": v(46.1, -28.58) * mm, "radius": 0.38 * mm});
            skCircle(sketch, "E244.MirrorC", {"center": v(42.07, -28.6) * mm, "radius": 0.38 * mm});
            skCircle(sketch, "E245.MirrorC", {"center": v(32.15, -38.5) * mm, "radius": 1.79 * mm});
            skCircle(sketch, "E246.MirrorC", {"center": v(30.04, -40.67) * mm, "radius": 0.38 * mm});
            skCircle(sketch, "E247.MirrorC", {"center": v(30.1, -36.51) * mm, "radius": 0.38 * mm});
            skCircle(sketch, "E248.MirrorC", {"center": v(34.17, -40.67) * mm, "radius": 0.38 * mm});
            skCircle(sketch, "E249.MirrorC", {"center": v(34.13, -36.49) * mm, "radius": 0.38 * mm});
            skCircle(sketch, "E250.MirrorC", {"center": v(20.24, -26.6) * mm, "radius": 1.79 * mm});
            skCircle(sketch, "E251.MirrorC", {"center": v(22.35, -24.42) * mm, "radius": 0.38 * mm});
            skCircle(sketch, "E252.MirrorC", {"center": v(22.3, -28.58) * mm, "radius": 0.38 * mm});
            skCircle(sketch, "E253.MirrorC", {"center": v(18.26, -28.6) * mm, "radius": 0.38 * mm});
            skCircle(sketch, "E254.MirrorC", {"center": v(18.22, -24.42) * mm, "radius": 0.38 * mm});
            skSolve(sketch);
        }
        {
            var Q0;
            Q0=makeQuery(id+"F12.imprint","IMPRINT",FACE,{"disambiguationData":[TD([[makeQuery(id+"F12.imprint","IMPRINT",EDGE,{"derivedFrom":sQuery(id+"F12.wireOp",EDGE,"E250.MirrorC")}),-1.0]])]});
            var Q1;
            Q1=makeQuery(id+"F12.imprint","IMPRINT",FACE,{"disambiguationData":[TD([[makeQuery(id+"F12.imprint","IMPRINT",EDGE,{"derivedFrom":sQuery(id+"F12.wireOp",EDGE,"E230")}),1.0]])]});
            var Q2;
            Q2=makeQuery(id+"F12.imprint","IMPRINT",FACE,{"disambiguationData":[TD([[makeQuery(id+"F12.imprint","IMPRINT",EDGE,{"derivedFrom":sQuery(id+"F12.wireOp",EDGE,"E235.MirrorC")}),-1.0]])]});
            var Q3;
            Q3=makeQuery(id+"F12.imprint","IMPRINT",FACE,{"disambiguationData":[TD([[makeQuery(id+"F12.imprint","IMPRINT",EDGE,{"derivedFrom":sQuery(id+"F12.wireOp",EDGE,"E240.MirrorC")}),-1.0]])]});
            var Q4;
            Q4=makeQuery(id+"F12.imprint","IMPRINT",FACE,{"disambiguationData":[TD([[makeQuery(id+"F12.imprint","IMPRINT",EDGE,{"derivedFrom":sQuery(id+"F12.wireOp",EDGE,"E245.MirrorC")}),-1.0]])]});
            extrude(context, id + "F13", {"entities" : qUnion([Q0, Q1, Q2, Q3, Q4]), "operationType" : NewBodyOperationType.ADD, "depth" : 3.17 * mm});
        }
        {
            var Q0;
            Q0=makeQuery(id+"F12.imprint","IMPRINT",FACE,{"disambiguationData":[TD([[makeQuery(id+"F12.imprint","IMPRINT",EDGE,{"derivedFrom":sQuery(id+"F12.wireOp",EDGE,"E253.MirrorC")}),-1.0]])]});
            var Q1;
            Q1=makeQuery(id+"F12.imprint","IMPRINT",FACE,{"disambiguationData":[TD([[makeQuery(id+"F12.imprint","IMPRINT",EDGE,{"derivedFrom":sQuery(id+"F12.wireOp",EDGE,"E254.MirrorC")}),-1.0]])]});
            var Q2;
            Q2=makeQuery(id+"F12.imprint","IMPRINT",FACE,{"disambiguationData":[TD([[makeQuery(id+"F12.imprint","IMPRINT",EDGE,{"derivedFrom":sQuery(id+"F12.wireOp",EDGE,"E251.MirrorC")}),-1.0]])]});
            var Q3;
            Q3=makeQuery(id+"F12.imprint","IMPRINT",FACE,{"disambiguationData":[TD([[makeQuery(id+"F12.imprint","IMPRINT",EDGE,{"derivedFrom":sQuery(id+"F12.wireOp",EDGE,"E252.MirrorC")}),-1.0]])]});
            var Q4;
            Q4=makeQuery(id+"F12.imprint","IMPRINT",FACE,{"disambiguationData":[TD([[makeQuery(id+"F12.imprint","IMPRINT",EDGE,{"derivedFrom":sQuery(id+"F12.wireOp",EDGE,"E234.1.0.0")}),1.0]])]});
            var Q5;
            Q5=makeQuery(id+"F12.imprint","IMPRINT",FACE,{"disambiguationData":[TD([[makeQuery(id+"F12.imprint","IMPRINT",EDGE,{"derivedFrom":sQuery(id+"F12.wireOp",EDGE,"E231")}),1.0]])]});
            var Q6;
            Q6=makeQuery(id+"F12.imprint","IMPRINT",FACE,{"disambiguationData":[TD([[makeQuery(id+"F12.imprint","IMPRINT",EDGE,{"derivedFrom":sQuery(id+"F12.wireOp",EDGE,"E232.1.0.0")}),1.0]])]});
            var Q7;
            Q7=makeQuery(id+"F12.imprint","IMPRINT",FACE,{"disambiguationData":[TD([[makeQuery(id+"F12.imprint","IMPRINT",EDGE,{"derivedFrom":sQuery(id+"F12.wireOp",EDGE,"E233.1.0.0")}),1.0]])]});
            var Q8;
            Q8=makeQuery(id+"F12.imprint","IMPRINT",FACE,{"disambiguationData":[TD([[makeQuery(id+"F12.imprint","IMPRINT",EDGE,{"derivedFrom":sQuery(id+"F12.wireOp",EDGE,"E247.MirrorC")}),-1.0]])]});
            var Q9;
            Q9=makeQuery(id+"F12.imprint","IMPRINT",FACE,{"disambiguationData":[TD([[makeQuery(id+"F12.imprint","IMPRINT",EDGE,{"derivedFrom":sQuery(id+"F12.wireOp",EDGE,"E246.MirrorC")}),-1.0]])]});
            var Q10;
            Q10=makeQuery(id+"F12.imprint","IMPRINT",FACE,{"disambiguationData":[TD([[makeQuery(id+"F12.imprint","IMPRINT",EDGE,{"derivedFrom":sQuery(id+"F12.wireOp",EDGE,"E248.MirrorC")}),-1.0]])]});
            var Q11;
            Q11=makeQuery(id+"F12.imprint","IMPRINT",FACE,{"disambiguationData":[TD([[makeQuery(id+"F12.imprint","IMPRINT",EDGE,{"derivedFrom":sQuery(id+"F12.wireOp",EDGE,"E249.MirrorC")}),-1.0]])]});
            var Q12;
            Q12=makeQuery(id+"F12.imprint","IMPRINT",FACE,{"disambiguationData":[TD([[makeQuery(id+"F12.imprint","IMPRINT",EDGE,{"derivedFrom":sQuery(id+"F12.wireOp",EDGE,"E244.MirrorC")}),-1.0]])]});
            var Q13;
            Q13=makeQuery(id+"F12.imprint","IMPRINT",FACE,{"disambiguationData":[TD([[makeQuery(id+"F12.imprint","IMPRINT",EDGE,{"derivedFrom":sQuery(id+"F12.wireOp",EDGE,"E241.MirrorC")}),-1.0]])]});
            var Q14;
            Q14=makeQuery(id+"F12.imprint","IMPRINT",FACE,{"disambiguationData":[TD([[makeQuery(id+"F12.imprint","IMPRINT",EDGE,{"derivedFrom":sQuery(id+"F12.wireOp",EDGE,"E242.MirrorC")}),-1.0]])]});
            var Q15;
            Q15=makeQuery(id+"F12.imprint","IMPRINT",FACE,{"disambiguationData":[TD([[makeQuery(id+"F12.imprint","IMPRINT",EDGE,{"derivedFrom":sQuery(id+"F12.wireOp",EDGE,"E243.MirrorC")}),-1.0]])]});
            var Q16;
            Q16=makeQuery(id+"F12.imprint","IMPRINT",FACE,{"disambiguationData":[TD([[makeQuery(id+"F12.imprint","IMPRINT",EDGE,{"derivedFrom":sQuery(id+"F12.wireOp",EDGE,"E237.MirrorC")}),-1.0]])]});
            var Q17;
            Q17=makeQuery(id+"F12.imprint","IMPRINT",FACE,{"disambiguationData":[TD([[makeQuery(id+"F12.imprint","IMPRINT",EDGE,{"derivedFrom":sQuery(id+"F12.wireOp",EDGE,"E236.MirrorC")}),-1.0]])]});
            var Q18;
            Q18=makeQuery(id+"F12.imprint","IMPRINT",FACE,{"disambiguationData":[TD([[makeQuery(id+"F12.imprint","IMPRINT",EDGE,{"derivedFrom":sQuery(id+"F12.wireOp",EDGE,"E239.MirrorC")}),-1.0]])]});
            var Q19;
            Q19=makeQuery(id+"F12.imprint","IMPRINT",FACE,{"disambiguationData":[TD([[makeQuery(id+"F12.imprint","IMPRINT",EDGE,{"derivedFrom":sQuery(id+"F12.wireOp",EDGE,"E238.MirrorC")}),-1.0]])]});
            extrude(context, id + "F14", {"entities" : qUnion([Q0, Q1, Q2, Q3, Q4, Q5, Q6, Q7, Q8, Q9, Q10, Q11, Q12, Q13, Q14, Q15, Q16, Q17, Q18, Q19]), "operationType" : NewBodyOperationType.ADD, "depth" : 0.2 * mm});
        }
        {
            var Q0;
            Q0=makeQuery(id+"F1.opExtrude","CAP_FACE",FACE,{"disambiguationData":[OSD([sQuery(id+"F0.wireOp",EDGE,"E0.bottom"),sQuery(id+"F0.wireOp",EDGE,"E0.top"),sQuery(id+"F0.wireOp",EDGE,"E0.left"),sQuery(id+"F0.wireOp",EDGE,"E0.right"),sQuery(id+"F0.wireOp",EDGE,"E1"),sQuery(id+"F0.wireOp",EDGE,"E2"),sQuery(id+"F0.wireOp",EDGE,"E3"),sQuery(id+"F0.wireOp",EDGE,"E4"),sQuery(id+"F0.wireOp",EDGE,"E8.MirrorC"),sQuery(id+"F0.wireOp",EDGE,"E9"),sQuery(id+"F0.wireOp",EDGE,"E11.MirrorC")])],"isStart":true});
            var sketch = newSketch(context, id + "F15", { "sketchPlane" : qUnion([Q0])});
            skLineSegment(sketch, "E255", {"start": v(62.9, 51.95) * mm, "end": v(62.9, 50.4) * mm, "construction": true});
            skLineSegment(sketch, "E256", {"start": v(62.12, 51.2) * mm, "end": v(63.72, 51.2) * mm, "construction": true});
            skLineSegment(sketch, "E257.bottom", {"start": v(63.02, 51.07) * mm, "end": v(62.77, 51.07) * mm});
            skLineSegment(sketch, "E257.top", {"start": v(63.02, 51.33) * mm, "end": v(62.77, 51.33) * mm});
            skLineSegment(sketch, "E257.left", {"start": v(63.02, 51.07) * mm, "end": v(63.02, 51.33) * mm});
            skLineSegment(sketch, "E257.right", {"start": v(62.77, 51.07) * mm, "end": v(62.77, 51.33) * mm});
            skPoint(sketch, "E257.middle", {"position": v(62.9, 51.2) * mm});
            skLineSegment(sketch, "E258", {"start": v(61.68, 51.98) * mm, "end": v(61.68, 50.4) * mm, "construction": true});
            skLineSegment(sketch, "E259.MirrorCS", {"start": v(60.6, 51.07) * mm, "end": v(60.6, 51.33) * mm});
            skLineSegment(sketch, "E260.MirrorCS", {"start": v(60.35, 51.33) * mm, "end": v(60.6, 51.33) * mm});
            skLineSegment(sketch, "E261.MirrorCS", {"start": v(60.35, 51.07) * mm, "end": v(60.6, 51.07) * mm});
            skLineSegment(sketch, "E262.MirrorCS", {"start": v(60.35, 51.07) * mm, "end": v(60.35, 51.33) * mm});
            skLineSegment(sketch, "E263", {"start": v(59.25, 51.98) * mm, "end": v(59.25, 50.38) * mm, "construction": true});
            skLineSegment(sketch, "E264.MirrorCS", {"start": v(58.14, 51.07) * mm, "end": v(58.14, 51.33) * mm});
            skLineSegment(sketch, "E265.MirrorCS", {"start": v(58.14, 51.33) * mm, "end": v(57.9, 51.33) * mm});
            skLineSegment(sketch, "E266.MirrorCS", {"start": v(57.9, 51.07) * mm, "end": v(57.9, 51.33) * mm});
            skLineSegment(sketch, "E267.MirrorCS", {"start": v(58.14, 51.07) * mm, "end": v(57.9, 51.07) * mm});
            skLineSegment(sketch, "E268.MirrorCS", {"start": v(55.72, 51.07) * mm, "end": v(55.72, 51.33) * mm});
            skLineSegment(sketch, "E269.MirrorCS", {"start": v(55.48, 51.33) * mm, "end": v(55.72, 51.33) * mm});
            skLineSegment(sketch, "E270.MirrorCS", {"start": v(55.48, 51.07) * mm, "end": v(55.48, 51.33) * mm});
            skLineSegment(sketch, "E271.MirrorCS", {"start": v(55.48, 51.07) * mm, "end": v(55.72, 51.07) * mm});
            skLineSegment(sketch, "E272", {"start": v(54.37, 51.98) * mm, "end": v(54.37, 50.4) * mm, "construction": true});
            skLineSegment(sketch, "E273.MirrorCS", {"start": v(53.26, 51.33) * mm, "end": v(53.02, 51.33) * mm});
            skLineSegment(sketch, "E274.MirrorCS", {"start": v(53.26, 51.07) * mm, "end": v(53.26, 51.33) * mm});
            skLineSegment(sketch, "E275.MirrorCS", {"start": v(53.26, 51.07) * mm, "end": v(53.02, 51.07) * mm});
            skLineSegment(sketch, "E276.MirrorCS", {"start": v(53.02, 51.07) * mm, "end": v(53.02, 51.33) * mm});
            skLineSegment(sketch, "E277.MirrorCS", {"start": v(50.84, 51.07) * mm, "end": v(50.84, 51.33) * mm});
            skLineSegment(sketch, "E278.MirrorCS", {"start": v(50.6, 51.33) * mm, "end": v(50.84, 51.33) * mm});
            skLineSegment(sketch, "E279.MirrorCS", {"start": v(50.6, 51.07) * mm, "end": v(50.84, 51.07) * mm});
            skLineSegment(sketch, "E280.MirrorCS", {"start": v(50.6, 51.07) * mm, "end": v(50.6, 51.33) * mm});
            skLineSegment(sketch, "E281", {"start": v(48.02, 52.9) * mm, "end": v(48.02, 49.48) * mm, "construction": true});
            skLineSegment(sketch, "E282.MirrorCS", {"start": v(45.43, 51.07) * mm, "end": v(45.43, 51.33) * mm});
            skLineSegment(sketch, "E283.MirrorCS", {"start": v(45.43, 51.33) * mm, "end": v(45.19, 51.33) * mm});
            skLineSegment(sketch, "E284.MirrorCS", {"start": v(45.19, 51.07) * mm, "end": v(45.19, 51.33) * mm});
            skLineSegment(sketch, "E285.MirrorCS", {"start": v(45.43, 51.07) * mm, "end": v(45.19, 51.07) * mm});
            skLineSegment(sketch, "E286.MirrorCS", {"start": v(42.77, 51.33) * mm, "end": v(43.01, 51.33) * mm});
            skLineSegment(sketch, "E287.MirrorCS", {"start": v(43.01, 51.07) * mm, "end": v(43.01, 51.33) * mm});
            skLineSegment(sketch, "E288.MirrorCS", {"start": v(42.77, 51.07) * mm, "end": v(43.01, 51.07) * mm});
            skLineSegment(sketch, "E289.MirrorCS", {"start": v(42.77, 51.07) * mm, "end": v(42.77, 51.33) * mm});
            skLineSegment(sketch, "E290.MirrorCS", {"start": v(40.55, 51.33) * mm, "end": v(40.3, 51.33) * mm});
            skLineSegment(sketch, "E291.MirrorCS", {"start": v(40.55, 51.07) * mm, "end": v(40.55, 51.33) * mm});
            skLineSegment(sketch, "E292.MirrorCS", {"start": v(40.55, 51.07) * mm, "end": v(40.3, 51.07) * mm});
            skLineSegment(sketch, "E293.MirrorCS", {"start": v(40.3, 51.07) * mm, "end": v(40.3, 51.33) * mm});
            skLineSegment(sketch, "E294.MirrorCS", {"start": v(37.89, 51.33) * mm, "end": v(38.13, 51.33) * mm});
            skLineSegment(sketch, "E295.MirrorCS", {"start": v(38.13, 51.07) * mm, "end": v(38.13, 51.33) * mm});
            skLineSegment(sketch, "E296.MirrorCS", {"start": v(37.89, 51.07) * mm, "end": v(38.13, 51.07) * mm});
            skLineSegment(sketch, "E297.MirrorCS", {"start": v(37.89, 51.07) * mm, "end": v(37.89, 51.33) * mm});
            skLineSegment(sketch, "E298.MirrorCS", {"start": v(35.68, 51.33) * mm, "end": v(35.43, 51.33) * mm});
            skLineSegment(sketch, "E299.MirrorCS", {"start": v(35.68, 51.07) * mm, "end": v(35.68, 51.33) * mm});
            skLineSegment(sketch, "E300.MirrorCS", {"start": v(35.68, 51.07) * mm, "end": v(35.43, 51.07) * mm});
            skLineSegment(sketch, "E301.MirrorCS", {"start": v(35.43, 51.07) * mm, "end": v(35.43, 51.33) * mm});
            skLineSegment(sketch, "E302.MirrorCS", {"start": v(33.01, 51.33) * mm, "end": v(33.26, 51.33) * mm});
            skLineSegment(sketch, "E303.MirrorCS", {"start": v(33.26, 51.07) * mm, "end": v(33.26, 51.33) * mm});
            skLineSegment(sketch, "E304.MirrorCS", {"start": v(33.01, 51.07) * mm, "end": v(33.26, 51.07) * mm});
            skLineSegment(sketch, "E305.MirrorCS", {"start": v(33.01, 51.07) * mm, "end": v(33.01, 51.33) * mm});
            skSolve(sketch);
        }
        {
            var Q0;
            Q0=makeQuery(id+"F15.imprint","IMPRINT",FACE,{"disambiguationData":[TD([[makeQuery(id+"F15.imprint","IMPRINT",EDGE,{"derivedFrom":sQuery(id+"F15.wireOp",EDGE,"E302.MirrorCS")}),-1.0]])]});
            var Q1;
            Q1=makeQuery(id+"F15.imprint","IMPRINT",FACE,{"disambiguationData":[TD([[makeQuery(id+"F15.imprint","IMPRINT",EDGE,{"derivedFrom":sQuery(id+"F15.wireOp",EDGE,"E298.MirrorCS")}),1.0]])]});
            var Q2;
            Q2=makeQuery(id+"F15.imprint","IMPRINT",FACE,{"disambiguationData":[TD([[makeQuery(id+"F15.imprint","IMPRINT",EDGE,{"derivedFrom":sQuery(id+"F15.wireOp",EDGE,"E294.MirrorCS")}),-1.0]])]});
            var Q3;
            Q3=makeQuery(id+"F15.imprint","IMPRINT",FACE,{"disambiguationData":[TD([[makeQuery(id+"F15.imprint","IMPRINT",EDGE,{"derivedFrom":sQuery(id+"F15.wireOp",EDGE,"E290.MirrorCS")}),1.0]])]});
            var Q4;
            Q4=makeQuery(id+"F15.imprint","IMPRINT",FACE,{"disambiguationData":[TD([[makeQuery(id+"F15.imprint","IMPRINT",EDGE,{"derivedFrom":sQuery(id+"F15.wireOp",EDGE,"E286.MirrorCS")}),-1.0]])]});
            var Q5;
            Q5=makeQuery(id+"F15.imprint","IMPRINT",FACE,{"disambiguationData":[TD([[makeQuery(id+"F15.imprint","IMPRINT",EDGE,{"derivedFrom":sQuery(id+"F15.wireOp",EDGE,"E282.MirrorCS")}),1.0]])]});
            var Q6;
            Q6=makeQuery(id+"F15.imprint","IMPRINT",FACE,{"disambiguationData":[TD([[makeQuery(id+"F15.imprint","IMPRINT",EDGE,{"derivedFrom":sQuery(id+"F15.wireOp",EDGE,"E277.MirrorCS")}),1.0]])]});
            var Q7;
            Q7=makeQuery(id+"F15.imprint","IMPRINT",FACE,{"disambiguationData":[TD([[makeQuery(id+"F15.imprint","IMPRINT",EDGE,{"derivedFrom":sQuery(id+"F15.wireOp",EDGE,"E273.MirrorCS")}),1.0]])]});
            var Q8;
            Q8=makeQuery(id+"F15.imprint","IMPRINT",FACE,{"disambiguationData":[TD([[makeQuery(id+"F15.imprint","IMPRINT",EDGE,{"derivedFrom":sQuery(id+"F15.wireOp",EDGE,"E268.MirrorCS")}),1.0]])]});
            var Q9;
            Q9=makeQuery(id+"F15.imprint","IMPRINT",FACE,{"disambiguationData":[TD([[makeQuery(id+"F15.imprint","IMPRINT",EDGE,{"derivedFrom":sQuery(id+"F15.wireOp",EDGE,"E264.MirrorCS")}),1.0]])]});
            var Q10;
            Q10=makeQuery(id+"F15.imprint","IMPRINT",FACE,{"disambiguationData":[TD([[makeQuery(id+"F15.imprint","IMPRINT",EDGE,{"derivedFrom":sQuery(id+"F15.wireOp",EDGE,"E259.MirrorCS")}),1.0]])]});
            var Q11;
            Q11=makeQuery(id+"F15.imprint","IMPRINT",FACE,{"disambiguationData":[TD([[makeQuery(id+"F15.imprint","IMPRINT",EDGE,{"derivedFrom":sQuery(id+"F15.wireOp",EDGE,"E257.bottom")}),-1.0]])]});
            extrude(context, id + "F16", {"entities" : qUnion([Q0, Q1, Q2, Q3, Q4, Q5, Q6, Q7, Q8, Q9, Q10, Q11]), "operationType" : NewBodyOperationType.ADD, "depth" : 8.1 * mm});
        }
        {
            var Q0;
            Q0=makeQuery(id+"F1.opExtrude","CAP_FACE",FACE,{"disambiguationData":[OSD([sQuery(id+"F0.wireOp",EDGE,"E0.bottom"),sQuery(id+"F0.wireOp",EDGE,"E0.top"),sQuery(id+"F0.wireOp",EDGE,"E0.left"),sQuery(id+"F0.wireOp",EDGE,"E0.right"),sQuery(id+"F0.wireOp",EDGE,"E1"),sQuery(id+"F0.wireOp",EDGE,"E2"),sQuery(id+"F0.wireOp",EDGE,"E3"),sQuery(id+"F0.wireOp",EDGE,"E4"),sQuery(id+"F0.wireOp",EDGE,"E8.MirrorC"),sQuery(id+"F0.wireOp",EDGE,"E9"),sQuery(id+"F0.wireOp",EDGE,"E11.MirrorC")])],"isStart":true});
            var sketch = newSketch(context, id + "F17", { "sketchPlane" : qUnion([Q0])});
            skLineSegment(sketch, "E306", {"start": v(64.5, 2.8) * mm, "end": v(62.87, 2.8) * mm, "construction": true});
            skPoint(sketch, "E307.endSnap0", {"position": v(63.69, 2.8) * mm});
            skLineSegment(sketch, "E308", {"start": v(63.72, 2.06) * mm, "end": v(63.72, 3.61) * mm, "construction": true});
            skLineSegment(sketch, "E309.bottom", {"start": v(63.59, 2.93) * mm, "end": v(63.84, 2.93) * mm});
            skLineSegment(sketch, "E309.top", {"start": v(63.59, 2.68) * mm, "end": v(63.84, 2.68) * mm});
            skLineSegment(sketch, "E309.left", {"start": v(63.59, 2.93) * mm, "end": v(63.59, 2.68) * mm});
            skLineSegment(sketch, "E309.right", {"start": v(63.84, 2.93) * mm, "end": v(63.84, 2.68) * mm});
            skPoint(sketch, "E309.middle", {"position": v(63.72, 2.8) * mm});
            skLineSegment(sketch, "E310", {"start": v(62.43, 2) * mm, "end": v(62.43, 3.7) * mm, "construction": true});
            skLineSegment(sketch, "E311.MirrorCS", {"start": v(61.28, 2.93) * mm, "end": v(61.28, 2.68) * mm});
            skLineSegment(sketch, "E312.MirrorCS", {"start": v(61.28, 2.68) * mm, "end": v(61.02, 2.68) * mm});
            skLineSegment(sketch, "E313.MirrorCS", {"start": v(61.02, 2.93) * mm, "end": v(61.02, 2.68) * mm});
            skLineSegment(sketch, "E314.MirrorCS", {"start": v(61.28, 2.93) * mm, "end": v(61.02, 2.93) * mm});
            skLineSegment(sketch, "E315", {"start": v(59.87, 1.86) * mm, "end": v(59.87, 3.72) * mm, "construction": true});
            skLineSegment(sketch, "E316.MirrorCS", {"start": v(58.46, 2.68) * mm, "end": v(58.71, 2.68) * mm});
            skLineSegment(sketch, "E317.MirrorCS", {"start": v(58.46, 2.93) * mm, "end": v(58.46, 2.68) * mm});
            skLineSegment(sketch, "E318.MirrorCS", {"start": v(58.46, 2.93) * mm, "end": v(58.71, 2.93) * mm});
            skLineSegment(sketch, "E319.MirrorCS", {"start": v(58.71, 2.93) * mm, "end": v(58.71, 2.68) * mm});
            skLineSegment(sketch, "E320.MirrorCS", {"start": v(56.15, 2.93) * mm, "end": v(56.15, 2.68) * mm});
            skLineSegment(sketch, "E321.MirrorCS", {"start": v(56.15, 2.68) * mm, "end": v(55.9, 2.68) * mm});
            skLineSegment(sketch, "E322.MirrorCS", {"start": v(55.9, 2.93) * mm, "end": v(55.9, 2.68) * mm});
            skLineSegment(sketch, "E323.MirrorCS", {"start": v(56.15, 2.93) * mm, "end": v(55.9, 2.93) * mm});
            skLineSegment(sketch, "E324", {"start": v(54.74, 1.86) * mm, "end": v(54.74, 3.76) * mm, "construction": true});
            skLineSegment(sketch, "E325.MirrorCS", {"start": v(53.58, 2.93) * mm, "end": v(53.58, 2.68) * mm});
            skLineSegment(sketch, "E326.MirrorCS", {"start": v(53.33, 2.68) * mm, "end": v(53.58, 2.68) * mm});
            skLineSegment(sketch, "E327.MirrorCS", {"start": v(53.33, 2.93) * mm, "end": v(53.33, 2.68) * mm});
            skLineSegment(sketch, "E328.MirrorCS", {"start": v(53.33, 2.93) * mm, "end": v(53.58, 2.93) * mm});
            skLineSegment(sketch, "E329.MirrorCS", {"start": v(51.02, 2.93) * mm, "end": v(51.02, 2.68) * mm});
            skLineSegment(sketch, "E330.MirrorCS", {"start": v(51.02, 2.68) * mm, "end": v(50.76, 2.68) * mm});
            skLineSegment(sketch, "E331.MirrorCS", {"start": v(50.76, 2.93) * mm, "end": v(50.76, 2.68) * mm});
            skLineSegment(sketch, "E332.MirrorCS", {"start": v(51.02, 2.93) * mm, "end": v(50.76, 2.93) * mm});
            skLineSegment(sketch, "E333.MirrorCS", {"start": v(48.45, 2.93) * mm, "end": v(48.45, 2.68) * mm});
            skLineSegment(sketch, "E334.MirrorCS", {"start": v(48.2, 2.68) * mm, "end": v(48.45, 2.68) * mm});
            skLineSegment(sketch, "E335.MirrorCS", {"start": v(48.2, 2.93) * mm, "end": v(48.2, 2.68) * mm});
            skLineSegment(sketch, "E336.MirrorCS", {"start": v(48.2, 2.93) * mm, "end": v(48.45, 2.93) * mm});
            skLineSegment(sketch, "E337.MirrorCS", {"start": v(45.63, 2.93) * mm, "end": v(45.63, 2.68) * mm});
            skLineSegment(sketch, "E338.MirrorCS", {"start": v(45.89, 2.68) * mm, "end": v(45.63, 2.68) * mm});
            skLineSegment(sketch, "E339.MirrorCS", {"start": v(45.89, 2.93) * mm, "end": v(45.89, 2.68) * mm});
            skLineSegment(sketch, "E340.MirrorCS", {"start": v(45.89, 2.93) * mm, "end": v(45.63, 2.93) * mm});
            skLineSegment(sketch, "E341", {"start": v(43.67, 0.97) * mm, "end": v(43.67, 4.86) * mm, "construction": true});
            skLineSegment(sketch, "E342.MirrorCS", {"start": v(41.7, 2.93) * mm, "end": v(41.7, 2.68) * mm});
            skLineSegment(sketch, "E343.MirrorCS", {"start": v(41.45, 2.68) * mm, "end": v(41.7, 2.68) * mm});
            skLineSegment(sketch, "E344.MirrorCS", {"start": v(41.45, 2.93) * mm, "end": v(41.45, 2.68) * mm});
            skLineSegment(sketch, "E345.MirrorCS", {"start": v(41.45, 2.93) * mm, "end": v(41.7, 2.93) * mm});
            skLineSegment(sketch, "E346.MirrorCS", {"start": v(39.14, 2.93) * mm, "end": v(39.14, 2.68) * mm});
            skLineSegment(sketch, "E347.MirrorCS", {"start": v(39.14, 2.68) * mm, "end": v(38.89, 2.68) * mm});
            skLineSegment(sketch, "E348.MirrorCS", {"start": v(38.89, 2.93) * mm, "end": v(38.89, 2.68) * mm});
            skLineSegment(sketch, "E349.MirrorCS", {"start": v(39.14, 2.93) * mm, "end": v(38.89, 2.93) * mm});
            skLineSegment(sketch, "E350.MirrorCS", {"start": v(36.58, 2.93) * mm, "end": v(36.58, 2.68) * mm});
            skLineSegment(sketch, "E351.MirrorCS", {"start": v(36.32, 2.68) * mm, "end": v(36.58, 2.68) * mm});
            skLineSegment(sketch, "E352.MirrorCS", {"start": v(36.32, 2.93) * mm, "end": v(36.32, 2.68) * mm});
            skLineSegment(sketch, "E353.MirrorCS", {"start": v(36.32, 2.93) * mm, "end": v(36.58, 2.93) * mm});
            skLineSegment(sketch, "E354.MirrorCS", {"start": v(34.01, 2.93) * mm, "end": v(34.01, 2.68) * mm});
            skLineSegment(sketch, "E355.MirrorCS", {"start": v(34.01, 2.68) * mm, "end": v(33.76, 2.68) * mm});
            skLineSegment(sketch, "E356.MirrorCS", {"start": v(33.76, 2.93) * mm, "end": v(33.76, 2.68) * mm});
            skLineSegment(sketch, "E357.MirrorCS", {"start": v(34.01, 2.93) * mm, "end": v(33.76, 2.93) * mm});
            skLineSegment(sketch, "E358.MirrorCS", {"start": v(31.45, 2.93) * mm, "end": v(31.45, 2.68) * mm});
            skLineSegment(sketch, "E359.MirrorCS", {"start": v(31.2, 2.68) * mm, "end": v(31.45, 2.68) * mm});
            skLineSegment(sketch, "E360.MirrorCS", {"start": v(31.2, 2.93) * mm, "end": v(31.2, 2.68) * mm});
            skLineSegment(sketch, "E361.MirrorCS", {"start": v(31.2, 2.93) * mm, "end": v(31.45, 2.93) * mm});
            skLineSegment(sketch, "E362.MirrorCS", {"start": v(28.88, 2.93) * mm, "end": v(28.88, 2.68) * mm});
            skLineSegment(sketch, "E363.MirrorCS", {"start": v(28.88, 2.68) * mm, "end": v(28.63, 2.68) * mm});
            skLineSegment(sketch, "E364.MirrorCS", {"start": v(28.63, 2.93) * mm, "end": v(28.63, 2.68) * mm});
            skLineSegment(sketch, "E365.MirrorCS", {"start": v(28.88, 2.93) * mm, "end": v(28.63, 2.93) * mm});
            skLineSegment(sketch, "E366.MirrorCS", {"start": v(26.31, 2.93) * mm, "end": v(26.31, 2.68) * mm});
            skLineSegment(sketch, "E367.MirrorCS", {"start": v(26.06, 2.68) * mm, "end": v(26.31, 2.68) * mm});
            skLineSegment(sketch, "E368.MirrorCS", {"start": v(26.06, 2.93) * mm, "end": v(26.06, 2.68) * mm});
            skLineSegment(sketch, "E369.MirrorCS", {"start": v(26.06, 2.93) * mm, "end": v(26.31, 2.93) * mm});
            skLineSegment(sketch, "E370.MirrorCS", {"start": v(23.75, 2.93) * mm, "end": v(23.75, 2.68) * mm});
            skLineSegment(sketch, "E371.MirrorCS", {"start": v(23.75, 2.68) * mm, "end": v(23.5, 2.68) * mm});
            skLineSegment(sketch, "E372.MirrorCS", {"start": v(23.5, 2.93) * mm, "end": v(23.5, 2.68) * mm});
            skLineSegment(sketch, "E373.MirrorCS", {"start": v(23.75, 2.93) * mm, "end": v(23.5, 2.93) * mm});
            skSolve(sketch);
        }
        {
            var Q0;
            Q0=makeQuery(id+"F17.imprint","IMPRINT",FACE,{"disambiguationData":[TD([[makeQuery(id+"F17.imprint","IMPRINT",EDGE,{"derivedFrom":sQuery(id+"F17.wireOp",EDGE,"E309.bottom")}),-1.0]])]});
            var Q1;
            Q1=makeQuery(id+"F17.imprint","IMPRINT",FACE,{"disambiguationData":[TD([[makeQuery(id+"F17.imprint","IMPRINT",EDGE,{"derivedFrom":sQuery(id+"F17.wireOp",EDGE,"E311.MirrorCS")}),-1.0]])]});
            var Q2;
            Q2=makeQuery(id+"F17.imprint","IMPRINT",FACE,{"disambiguationData":[TD([[makeQuery(id+"F17.imprint","IMPRINT",EDGE,{"derivedFrom":sQuery(id+"F17.wireOp",EDGE,"E316.MirrorCS")}),1.0]])]});
            var Q3;
            Q3=makeQuery(id+"F17.imprint","IMPRINT",FACE,{"disambiguationData":[TD([[makeQuery(id+"F17.imprint","IMPRINT",EDGE,{"derivedFrom":sQuery(id+"F17.wireOp",EDGE,"E320.MirrorCS")}),-1.0]])]});
            var Q4;
            Q4=makeQuery(id+"F17.imprint","IMPRINT",FACE,{"disambiguationData":[TD([[makeQuery(id+"F17.imprint","IMPRINT",EDGE,{"derivedFrom":sQuery(id+"F17.wireOp",EDGE,"E325.MirrorCS")}),-1.0]])]});
            var Q5;
            Q5=makeQuery(id+"F17.imprint","IMPRINT",FACE,{"disambiguationData":[TD([[makeQuery(id+"F17.imprint","IMPRINT",EDGE,{"derivedFrom":sQuery(id+"F17.wireOp",EDGE,"E329.MirrorCS")}),-1.0]])]});
            var Q6;
            Q6=makeQuery(id+"F17.imprint","IMPRINT",FACE,{"disambiguationData":[TD([[makeQuery(id+"F17.imprint","IMPRINT",EDGE,{"derivedFrom":sQuery(id+"F17.wireOp",EDGE,"E333.MirrorCS")}),-1.0]])]});
            var Q7;
            Q7=makeQuery(id+"F17.imprint","IMPRINT",FACE,{"disambiguationData":[TD([[makeQuery(id+"F17.imprint","IMPRINT",EDGE,{"derivedFrom":sQuery(id+"F17.wireOp",EDGE,"E337.MirrorCS")}),1.0]])]});
            var Q8;
            Q8=makeQuery(id+"F17.imprint","IMPRINT",FACE,{"disambiguationData":[TD([[makeQuery(id+"F17.imprint","IMPRINT",EDGE,{"derivedFrom":sQuery(id+"F17.wireOp",EDGE,"E342.MirrorCS")}),-1.0]])]});
            var Q9;
            Q9=makeQuery(id+"F17.imprint","IMPRINT",FACE,{"disambiguationData":[TD([[makeQuery(id+"F17.imprint","IMPRINT",EDGE,{"derivedFrom":sQuery(id+"F17.wireOp",EDGE,"E346.MirrorCS")}),-1.0]])]});
            var Q10;
            Q10=makeQuery(id+"F17.imprint","IMPRINT",FACE,{"disambiguationData":[TD([[makeQuery(id+"F17.imprint","IMPRINT",EDGE,{"derivedFrom":sQuery(id+"F17.wireOp",EDGE,"E350.MirrorCS")}),-1.0]])]});
            var Q11;
            Q11=makeQuery(id+"F17.imprint","IMPRINT",FACE,{"disambiguationData":[TD([[makeQuery(id+"F17.imprint","IMPRINT",EDGE,{"derivedFrom":sQuery(id+"F17.wireOp",EDGE,"E354.MirrorCS")}),-1.0]])]});
            var Q12;
            Q12=makeQuery(id+"F17.imprint","IMPRINT",FACE,{"disambiguationData":[TD([[makeQuery(id+"F17.imprint","IMPRINT",EDGE,{"derivedFrom":sQuery(id+"F17.wireOp",EDGE,"E358.MirrorCS")}),-1.0]])]});
            var Q13;
            Q13=makeQuery(id+"F17.imprint","IMPRINT",FACE,{"disambiguationData":[TD([[makeQuery(id+"F17.imprint","IMPRINT",EDGE,{"derivedFrom":sQuery(id+"F17.wireOp",EDGE,"E362.MirrorCS")}),-1.0]])]});
            var Q14;
            Q14=makeQuery(id+"F17.imprint","IMPRINT",FACE,{"disambiguationData":[TD([[makeQuery(id+"F17.imprint","IMPRINT",EDGE,{"derivedFrom":sQuery(id+"F17.wireOp",EDGE,"E366.MirrorCS")}),-1.0]])]});
            var Q15;
            Q15=makeQuery(id+"F17.imprint","IMPRINT",FACE,{"disambiguationData":[TD([[makeQuery(id+"F17.imprint","IMPRINT",EDGE,{"derivedFrom":sQuery(id+"F17.wireOp",EDGE,"E370.MirrorCS")}),-1.0]])]});
            extrude(context, id + "F18", {"entities" : qUnion([Q0, Q1, Q2, Q3, Q4, Q5, Q6, Q7, Q8, Q9, Q10, Q11, Q12, Q13, Q14, Q15]), "operationType" : NewBodyOperationType.ADD, "depth" : 8.1 * mm});
        }
        {
            var Q0;
            {var subQ4=sQuery(id+"F0.wireOp",EDGE,"E0.top");var subQ6=sQuery(id+"F0.wireOp",EDGE,"E11.MirrorC");var subQ8=sQuery(id+"F0.wireOp",EDGE,"E9");var subQ10=sQuery(id+"F0.wireOp",EDGE,"E0.right");var subQ11=sQuery(id+"F0.wireOp",EDGE,"E0.bottom");var subQ12=sQuery(id+"F0.wireOp",EDGE,"E1");var subQ15=makeQuery(id+"F1.opExtrude","SWEPT_FACE",FACE,{"disambiguationData":[OSD([subQ11])]});var subQ16=sQuery(id+"F0.wireOp",EDGE,"E0.left");var subQ19=sQuery(id+"F0.wireOp",EDGE,"E4");var subQ23=sQuery(id+"F0.wireOp",EDGE,"E3");var subQ26=sQuery(id+"F0.wireOp",EDGE,"E2");var subQ29=sQuery(id+"F0.wireOp",EDGE,"E8.MirrorC");Q0=makeQuery(id+"F5.boolean.opBoolean","SPLIT",FACE,{"disambiguationData":[TD([subQ15])],"derivedFrom":makeQuery(id+"F3.boolean.opBoolean","SPLIT",FACE,{"disambiguationData":[TD([subQ15])],"derivedFrom":makeQuery(id+"F1.opExtrude","CAP_FACE",FACE,{"disambiguationData":[OSD([subQ11,subQ4,subQ16,subQ10,subQ12,subQ26,subQ23,subQ19,subQ29,subQ8,subQ6])],"isStart":false})})});}
            var sketch = newSketch(context, id + "F19", { "sketchPlane" : qUnion([Q0])});
            skPoint(sketch, "E374", {"position": v(6.35, -10.32) * mm});
            skLineSegment(sketch, "E375", {"start": v(0, -26.99) * mm, "end": v(12.7, -26.99) * mm, "construction": true});
            skPoint(sketch, "E375.endSnap0", {"position": v(0, -26.99) * mm});
            skPoint(sketch, "E376.MirrorP", {"position": v(6.35, -43.66) * mm});
            skCircle(sketch, "E377", {"center": v(6.35, -10.32) * mm, "radius": 0.34 * mm});
            skCircle(sketch, "E378", {"center": v(6.35, -43.66) * mm, "radius": 0.34 * mm});
            skSolve(sketch);
        }
        {
            var Q0;
            Q0=makeQuery(id+"F19.imprint","IMPRINT",FACE,{"disambiguationData":[TD([[makeQuery(id+"F19.imprint","IMPRINT",EDGE,{"derivedFrom":sQuery(id+"F19.wireOp",EDGE,"E378")}),1.0]])]});
            var Q1;
            Q1=makeQuery(id+"F19.imprint","IMPRINT",FACE,{"disambiguationData":[TD([[makeQuery(id+"F19.imprint","IMPRINT",EDGE,{"derivedFrom":sQuery(id+"F19.wireOp",EDGE,"E377")}),1.0]])]});
            extrude(context, id + "F20", {"entities" : qUnion([Q0, Q1]), "operationType" : NewBodyOperationType.REMOVE, "oppositeDirection" : true, "depth" : 1.6 * mm});
        }
    });
